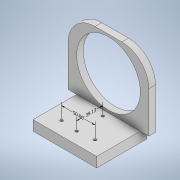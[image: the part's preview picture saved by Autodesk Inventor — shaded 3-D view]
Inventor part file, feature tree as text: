
AUTODESK INVENTOR PART (.ipt)
format: ipt  version: 2022 (Build 260153000, 153)  size: 165,376 bytes
history: native  units: mm
features: extrude x5, sketch x5, other x3, chamfer x1, fillet x1
ambient origin geometry x8: Origin, YZ Plane, XZ Plane, XY Plane, X Axis, Y Axis, Z Axis, Center Point
bodies: Solid1 (feature_tree)
feature tree (15):
  other  "Annotations"
  extrude  "Extrusion1"  Depth=75.0mm
  extrude  "Extrusion2"  Depth=12.7mm
  extrude  "Extrusion4"  Depth=9.906mm
  extrude  "Extrusion5"  Depth=101.6mm
  extrude  "Extrusion6"  TaperAngle=0.0deg  [1 undecoded]
  chamfer  "Chamfer1"  Distance=95.0mm
  fillet  "Fillet1"  [1 undecoded]
  sketch  "Sketch1"  dims[d0=94.996mm d1=75.0mm]
  sketch  "Sketch2"  dims[d2=15.0mm d3=0.0mm d4=12.7mm]
  sketch  "Sketch4"  dims[d5=12.7mm d6=9.906mm]
  sketch  "Sketch5"  dims[d7=101.6mm d8=0.0mm d12=4.0mm]
  sketch  "Sketch6"  dims[d13=4.0mm d14=0.0mm d15=0.0mm d17=95.0mm d18=0.0mm d19=0.0mm d23=4.0mm d24=0.0mm d25=0.0mm d26=2.0mm d27=2.0mm d28=45.0deg d30=40.25mm d16=39.126314mm d29=50.0mm]
  other  "Linear Dimension 1"
  other  "Linear Dimension 2"
note: 2 required parameter values undecoded (feature->parameter linkage not recoverable at this tier; creation-order binding heuristic only, values carry confidence <= 0.55)
